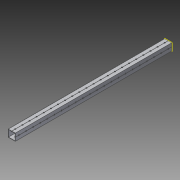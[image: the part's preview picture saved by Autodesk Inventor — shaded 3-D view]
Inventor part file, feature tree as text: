
AUTODESK INVENTOR PART (.ipt)
format: ipt  version: 2014 SP1 (Build 180222100, 222)  size: 1,278,976 bytes
history: native  units: in
note: dims shown in document units (in); Inventor stores cm internally (conversion verified against a paired STEP export)
features: pattern_circular x1, other x1, plane x1, extrude x1, imported_body x1, sketch x1
ambient origin geometry x8: Origin, YZ Plane, XZ Plane, XY Plane, X Axis, Y Axis, Z Axis, Center Point
bodies: Body1 (feature_tree)
feature tree (6):
  pattern_circular  "CirPattern2"
  other  "217-3426-STEP1"
  plane  "Work Plane1"
  extrude  "Extrusion1"  Depth=3937.0079in TaperAngle=0.0deg
  imported_body  "Base1"
  sketch  "Sketch1"  dims[d0=-22.0in d1=3937.0079in d2=0.0in]
